# Revit family: MAXIDRIVE MOTORISED RL300 MITRE.rfa)
name_source: partatom
category: Generic Models
revit_build: Autodesk Revit 2018 (Build: 20170223_1515(x64)
units: mm (PartAtom-declared; Revit-internal decimal feet)

## family parameters
Always vertical = Yes
Can host rebar = No
Cut with Voids When Loaded = No
Part Type = Normal
Room Calculation Point = No
Round Connector Dimension = Use Diameter
Shared = No
Work Plane-Based = No

## types (1)
- MAXIDRIVE MOTORISED RL300 MITRE.rfa)
    ANGLE = 0.00°
    ANGLE RESTRICTION = 0.00°
    ARM LENGTH = 654 mm  [stored 2.14567 ft]
    ARRAY = 2
    DRIVE ARM = <By Category>
    LENGTH = 960 mm
    MAXIDRIVE FRAME = <By Category>
    OFFSET = 20 mm  [stored 0.0656168 ft]
    REMAINDER = 1 mm  [stored 0.00328084 ft]
    RL300 MITRE END CAP = <By Category>
    RL300 MITRE LOUVRE BLADE = <By Category>
    SPACING = 307 mm  [stored 1.00722 ft]
    WIDTH = 1500 mm  [stored 4.92126 ft]

note: [stored X ft] marks values corroborated as IEEE doubles in the binary element streams (Revit-internal decimal feet)

## geometry (parser evidence)
native form markers: Sweep x23
no freeform markers — native parametric forms only
